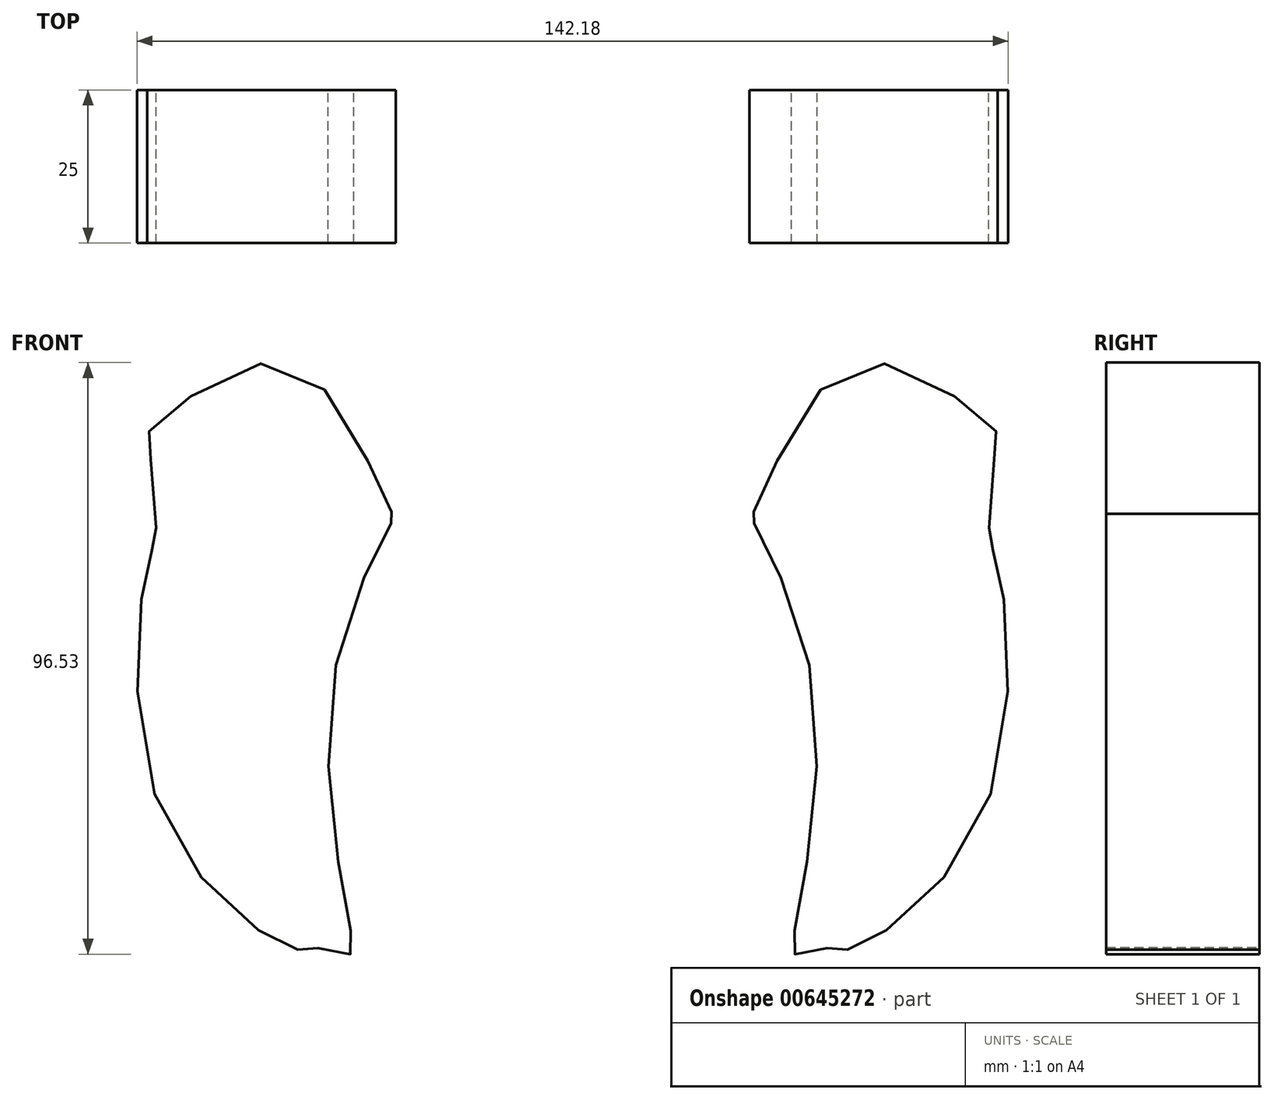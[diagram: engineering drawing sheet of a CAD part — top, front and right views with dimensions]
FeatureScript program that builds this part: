
annotation { "Feature Type Name" : "Feature", "Feature Type Description" : "" }
export const myFeature = defineFeature(function(context is Context, id is Id, definition is map)
    precondition{}
    {
        {
            var Q0;
            Q0=qCreatedBy(makeId("Front.planeOp"),FACE);
            var sketch = newSketch(context, id + "F0", { "sketchPlane" : qUnion([Q0])});
            skFitSpline(sketch, "E0", {"points": [v(-44.85, -43.93) * mm, v(-43.18, -43.55) * mm, v(-36.31, -44.67) * mm, v(-35.75, -43.74) * mm, v(-39.1, 0) * mm, v(-28.88, 27.2) * mm, v(-29.25, 27.2) * mm, v(-46.53, 51.54) * mm, v(-69.37, 40.4) * mm, v(-69.37, 40.21) * mm, v(-68.07, 21.64) * mm, v(-68.44, 21.45) * mm, v(-67.51, -20.52) * mm, v(-44.85, -43.93) * mm]});
            skSolve(sketch);
        }
        {
            var Q0;
            Q0=makeQuery(id+"F0.imprint","IMPRINT",FACE,{"disambiguationData":[TD([[makeQuery(id+"F0.imprint","IMPRINT",EDGE,{"derivedFrom":sQuery(id+"F0.wireOp",EDGE,"E0")}),1.0]])]});
            extrude(context, id + "F1", {"entities" : qUnion([Q0]), "depth" : 25 * mm, "offsetDistance" : 25 * mm});
        }
        {
            var Q0;
            Q0=makeQuery(id+"F1.opExtrude","SWEPT_BODY",BODY,{"disambiguationData":[OSD([sQuery(id+"F0.wireOp",EDGE,"E0")])]});
            var Q1;
            Q1=qCreatedBy(makeId("Right.planeOp"),FACE);
            mirror(context, id + "F2", {"entities" : qUnion([Q0]), "mirrorPlane" : qUnion([Q1])});
        }
    });
